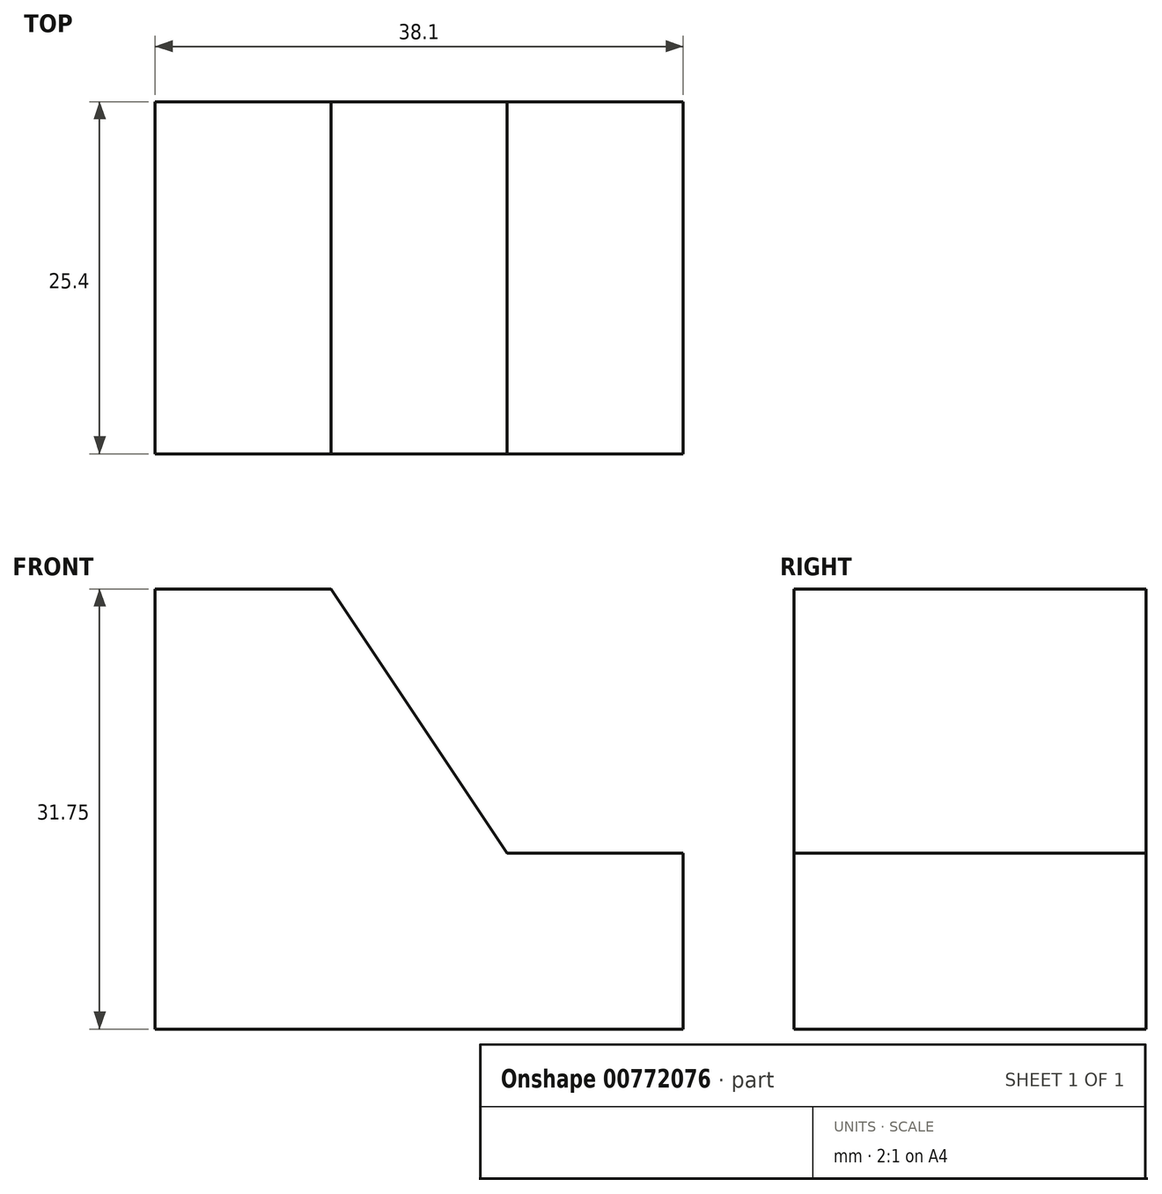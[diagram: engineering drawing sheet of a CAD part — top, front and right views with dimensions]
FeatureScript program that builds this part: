
annotation { "Feature Type Name" : "Feature", "Feature Type Description" : "" }
export const myFeature = defineFeature(function(context is Context, id is Id, definition is map)
    precondition{}
    {
        {
            var Q0;
            Q0=qCreatedBy(makeId("Front.planeOp"),FACE);
            var sketch = newSketch(context, id + "F0", { "sketchPlane" : qUnion([Q0])});
            skLineSegment(sketch, "E0", {"start": v(0, 0) * mm, "end": v(0, -31.75) * mm});
            skLineSegment(sketch, "E1", {"start": v(0, -31.75) * mm, "end": v(38.1, -31.75) * mm});
            skLineSegment(sketch, "E2", {"start": v(38.1, -31.75) * mm, "end": v(38.1, -19.05) * mm});
            skLineSegment(sketch, "E3", {"start": v(38.1, -19.05) * mm, "end": v(25.4, -19.05) * mm});
            skLineSegment(sketch, "E4", {"start": v(0, 0) * mm, "end": v(12.7, 0) * mm});
            skLineSegment(sketch, "E5", {"start": v(12.7, 0) * mm, "end": v(25.4, -19.05) * mm});
            skSolve(sketch);
        }
        {
            var Q0;
            Q0 = qSketchRegion(id + "F0", true);
            extrude(context, id + "F1", {"entities" : qUnion([Q0]), "depth" : 25.4 * mm, "offsetDistance" : 25.4 * mm});
        }
    });
